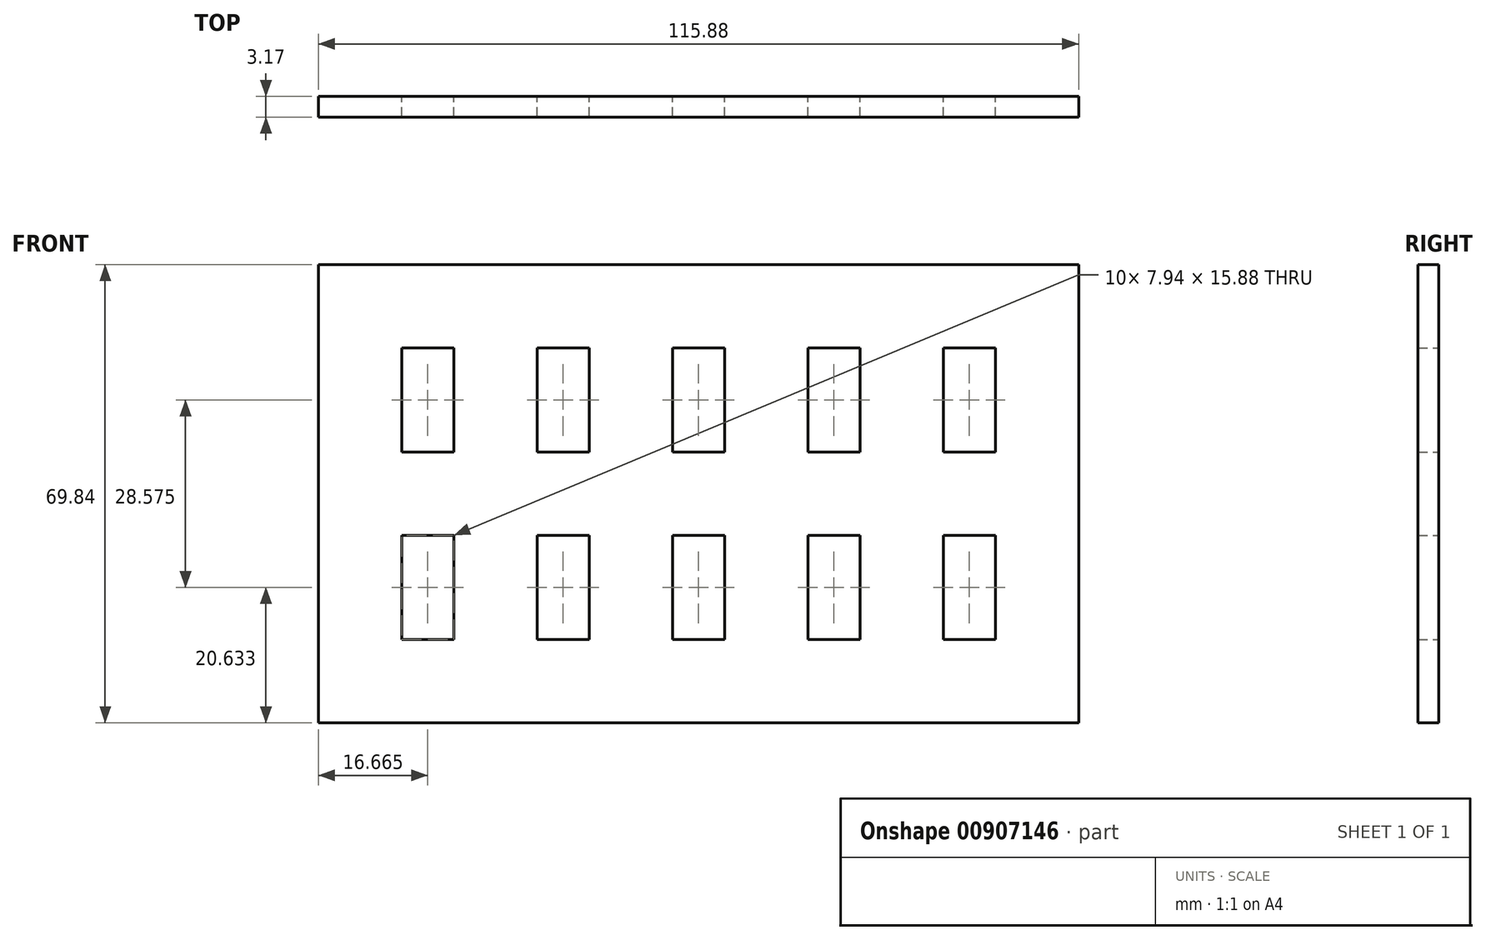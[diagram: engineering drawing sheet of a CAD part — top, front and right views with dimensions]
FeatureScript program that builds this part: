
annotation { "Feature Type Name" : "Feature", "Feature Type Description" : "" }
export const myFeature = defineFeature(function(context is Context, id is Id, definition is map)
    precondition{}
    {
        {
            var Q0;
            Q0=qCreatedBy(makeId("Front.planeOp"),FACE);
            var sketch = newSketch(context, id + "F0", { "sketchPlane" : qUnion([Q0])});
            skLineSegment(sketch, "E0.bottom", {"start": v(57.94, -34.92) * mm, "end": v(-57.94, -34.93) * mm});
            skLineSegment(sketch, "E0.top", {"start": v(57.94, 34.93) * mm, "end": v(-57.94, 34.92) * mm});
            skLineSegment(sketch, "E0.left", {"start": v(57.94, -34.92) * mm, "end": v(57.94, 34.93) * mm});
            skLineSegment(sketch, "E0.right", {"start": v(-57.94, -34.93) * mm, "end": v(-57.94, 34.93) * mm});
            skPoint(sketch, "E0.middle", {"position": v(0, 0) * mm});
            skLineSegment(sketch, "E1.bottom", {"start": v(-37.3, 6.35) * mm, "end": v(-45.24, 6.35) * mm});
            skLineSegment(sketch, "E1.top", {"start": v(-37.3, 22.22) * mm, "end": v(-45.24, 22.22) * mm});
            skLineSegment(sketch, "E1.left", {"start": v(-37.3, 6.35) * mm, "end": v(-37.3, 22.23) * mm});
            skLineSegment(sketch, "E1.right", {"start": v(-45.24, 6.35) * mm, "end": v(-45.24, 22.23) * mm});
            skPoint(sketch, "E1.middle", {"position": v(-41.27, 14.29) * mm});
            skLineSegment(sketch, "E2.0.1.0", {"start": v(-37.3, -22.23) * mm, "end": v(-45.24, -22.23) * mm});
            skLineSegment(sketch, "E2.0.1.1", {"start": v(-37.3, -6.35) * mm, "end": v(-45.24, -6.35) * mm});
            skLineSegment(sketch, "E2.0.1.2", {"start": v(-45.24, -22.22) * mm, "end": v(-45.24, -6.35) * mm});
            skLineSegment(sketch, "E2.0.1.3", {"start": v(-37.3, -22.22) * mm, "end": v(-37.3, -6.35) * mm});
            skPoint(sketch, "E2.0.1.4", {"position": v(-41.27, -14.29) * mm});
            skLineSegment(sketch, "E2.1.0.0", {"start": v(-16.67, 6.35) * mm, "end": v(-24.6, 6.35) * mm});
            skLineSegment(sketch, "E2.1.0.1", {"start": v(-16.67, 22.22) * mm, "end": v(-24.6, 22.22) * mm});
            skLineSegment(sketch, "E2.1.0.2", {"start": v(-24.6, 6.35) * mm, "end": v(-24.6, 22.23) * mm});
            skLineSegment(sketch, "E2.1.0.3", {"start": v(-16.67, 6.35) * mm, "end": v(-16.67, 22.23) * mm});
            skPoint(sketch, "E2.1.0.4", {"position": v(-20.64, 14.29) * mm});
            skLineSegment(sketch, "E2.1.1.0", {"start": v(-16.67, -22.23) * mm, "end": v(-24.6, -22.23) * mm});
            skLineSegment(sketch, "E2.1.1.1", {"start": v(-16.67, -6.35) * mm, "end": v(-24.6, -6.35) * mm});
            skLineSegment(sketch, "E2.1.1.2", {"start": v(-24.6, -22.23) * mm, "end": v(-24.6, -6.35) * mm});
            skLineSegment(sketch, "E2.1.1.3", {"start": v(-16.67, -22.22) * mm, "end": v(-16.67, -6.35) * mm});
            skPoint(sketch, "E2.1.1.4", {"position": v(-20.64, -14.29) * mm});
            skLineSegment(sketch, "E2.2.0.0", {"start": v(3.97, 6.35) * mm, "end": v(-3.97, 6.35) * mm});
            skLineSegment(sketch, "E2.2.0.1", {"start": v(3.97, 22.22) * mm, "end": v(-3.97, 22.22) * mm});
            skLineSegment(sketch, "E2.2.0.2", {"start": v(-3.97, 6.35) * mm, "end": v(-3.97, 22.23) * mm});
            skLineSegment(sketch, "E2.2.0.3", {"start": v(3.97, 6.35) * mm, "end": v(3.97, 22.23) * mm});
            skPoint(sketch, "E2.2.0.4", {"position": v(0, 14.29) * mm});
            skLineSegment(sketch, "E2.2.1.0", {"start": v(3.97, -22.23) * mm, "end": v(-3.97, -22.23) * mm});
            skLineSegment(sketch, "E2.2.1.1", {"start": v(3.97, -6.35) * mm, "end": v(-3.97, -6.35) * mm});
            skLineSegment(sketch, "E2.2.1.2", {"start": v(-3.97, -22.23) * mm, "end": v(-3.97, -6.35) * mm});
            skLineSegment(sketch, "E2.2.1.3", {"start": v(3.97, -22.22) * mm, "end": v(3.97, -6.35) * mm});
            skPoint(sketch, "E2.2.1.4", {"position": v(0, -14.29) * mm});
            skLineSegment(sketch, "E2.3.0.0", {"start": v(24.6, 6.35) * mm, "end": v(16.67, 6.35) * mm});
            skLineSegment(sketch, "E2.3.0.1", {"start": v(24.6, 22.22) * mm, "end": v(16.67, 22.22) * mm});
            skLineSegment(sketch, "E2.3.0.2", {"start": v(16.67, 6.35) * mm, "end": v(16.67, 22.23) * mm});
            skLineSegment(sketch, "E2.3.0.3", {"start": v(24.6, 6.35) * mm, "end": v(24.6, 22.23) * mm});
            skPoint(sketch, "E2.3.0.4", {"position": v(20.64, 14.29) * mm});
            skLineSegment(sketch, "E2.3.1.0", {"start": v(24.6, -22.23) * mm, "end": v(16.67, -22.23) * mm});
            skLineSegment(sketch, "E2.3.1.1", {"start": v(24.6, -6.35) * mm, "end": v(16.67, -6.35) * mm});
            skLineSegment(sketch, "E2.3.1.2", {"start": v(16.67, -22.23) * mm, "end": v(16.67, -6.35) * mm});
            skLineSegment(sketch, "E2.3.1.3", {"start": v(24.6, -22.22) * mm, "end": v(24.6, -6.35) * mm});
            skPoint(sketch, "E2.3.1.4", {"position": v(20.64, -14.29) * mm});
            skLineSegment(sketch, "E2.4.0.0", {"start": v(45.24, 6.35) * mm, "end": v(37.3, 6.35) * mm});
            skLineSegment(sketch, "E2.4.0.1", {"start": v(45.24, 22.22) * mm, "end": v(37.3, 22.22) * mm});
            skLineSegment(sketch, "E2.4.0.2", {"start": v(37.3, 6.35) * mm, "end": v(37.3, 22.23) * mm});
            skLineSegment(sketch, "E2.4.0.3", {"start": v(45.24, 6.35) * mm, "end": v(45.24, 22.23) * mm});
            skPoint(sketch, "E2.4.0.4", {"position": v(41.27, 14.29) * mm});
            skLineSegment(sketch, "E2.4.1.0", {"start": v(45.24, -22.23) * mm, "end": v(37.3, -22.23) * mm});
            skLineSegment(sketch, "E2.4.1.1", {"start": v(45.24, -6.35) * mm, "end": v(37.3, -6.35) * mm});
            skLineSegment(sketch, "E2.4.1.2", {"start": v(37.3, -22.23) * mm, "end": v(37.3, -6.35) * mm});
            skLineSegment(sketch, "E2.4.1.3", {"start": v(45.24, -22.23) * mm, "end": v(45.24, -6.35) * mm});
            skPoint(sketch, "E2.4.1.4", {"position": v(41.27, -14.29) * mm});
            skLineSegment(sketch, "E2.direction1", {"start": v(-45.24, 6.35) * mm, "end": v(-24.6, 6.35) * mm, "construction": true});
            skLineSegment(sketch, "E2.direction2", {"start": v(-45.24, 6.35) * mm, "end": v(-45.24, -22.22) * mm, "construction": true});
            skSolve(sketch);
        }
        {
            var Q0;
            Q0=makeQuery(id+"F0.imprint","IMPRINT",FACE,{"disambiguationData":[TD([[makeQuery(id+"F0.imprint","IMPRINT",EDGE,{"derivedFrom":sQuery(id+"F0.wireOp",EDGE,"E0.bottom")}),-1.0]])]});
            extrude(context, id + "F1", {"entities" : qUnion([Q0]), "depth" : 3.17 * mm, "offsetDistance" : 25.4 * mm});
        }
    });
